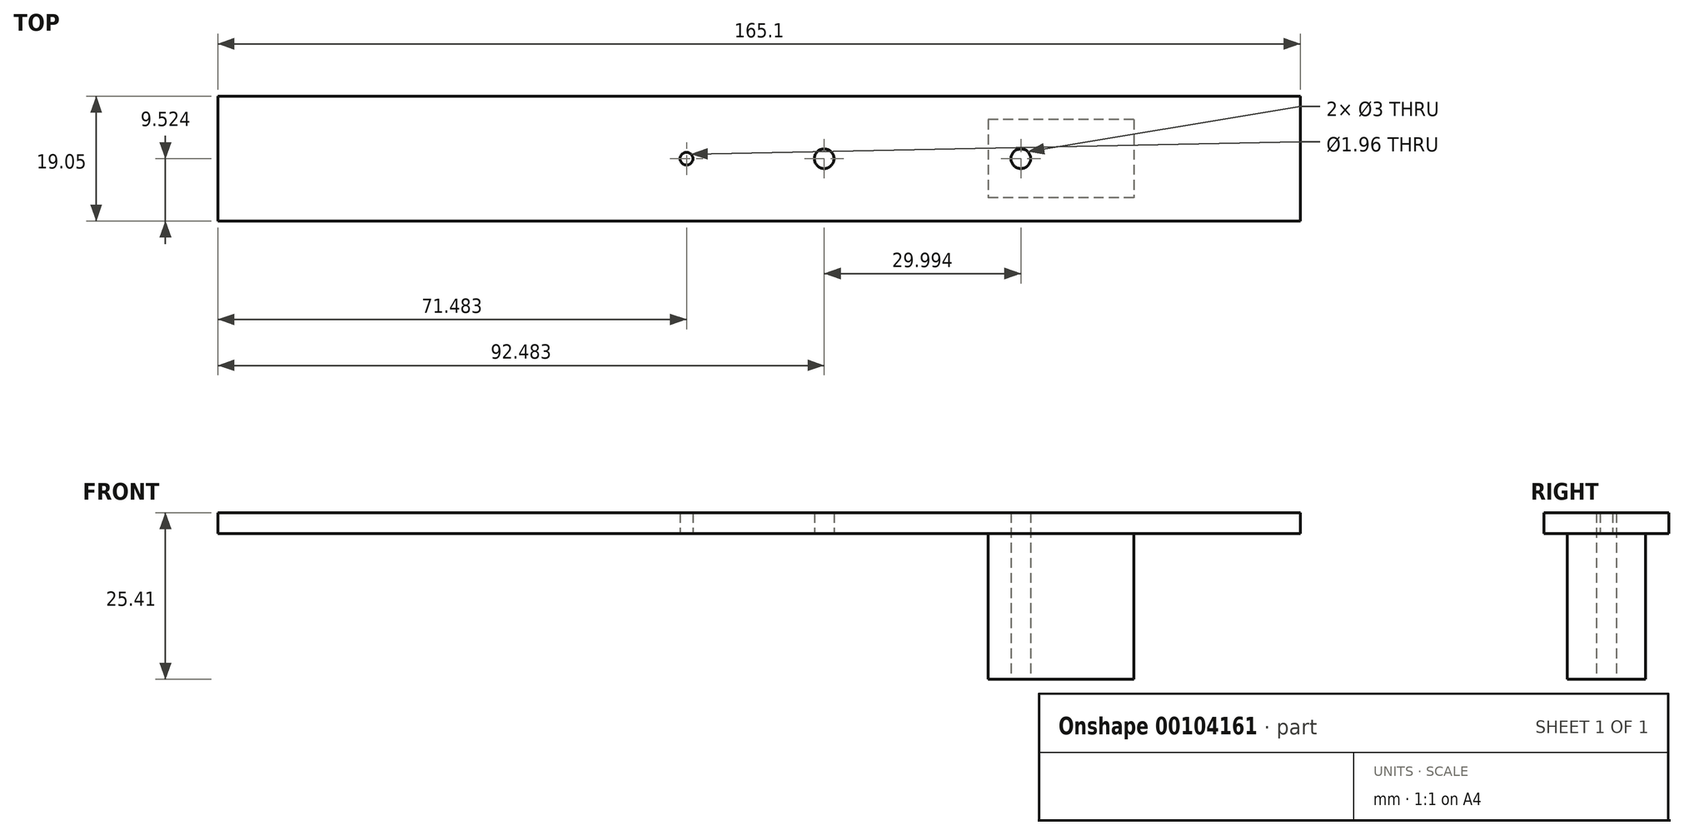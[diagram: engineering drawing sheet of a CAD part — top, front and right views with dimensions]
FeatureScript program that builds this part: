
annotation { "Feature Type Name" : "Feature", "Feature Type Description" : "" }
export const myFeature = defineFeature(function(context is Context, id is Id, definition is map)
    precondition{}
    {
        {
            var Q0;
            Q0=qCreatedBy(makeId("Top.planeOp"),FACE);
            var sketch = newSketch(context, id + "F0", { "sketchPlane" : qUnion([Q0])});
            skLineSegment(sketch, "E0.bottom", {"start": v(-131.62, -9.37) * mm, "end": v(33.48, -9.37) * mm});
            skLineSegment(sketch, "E0.top", {"start": v(-131.62, -28.42) * mm, "end": v(33.48, -28.42) * mm});
            skLineSegment(sketch, "E0.left", {"start": v(-131.62, -9.37) * mm, "end": v(-131.62, -28.42) * mm});
            skLineSegment(sketch, "E0.right", {"start": v(33.48, -9.37) * mm, "end": v(33.48, -28.42) * mm});
            skSolve(sketch);
        }
        {
            var Q0;
            Q0=makeQuery(id+"F0.imprint","IMPRINT",FACE,{"disambiguationData":[TD([[makeQuery(id+"F0.imprint","IMPRINT",EDGE,{"derivedFrom":sQuery(id+"F0.wireOp",EDGE,"E0.bottom")}),-1.0]])]});
            extrude(context, id + "F1", {"entities" : qUnion([Q0]), "depth" : 3.17 * mm});
        }
        {
            var Q0;
            Q0=makeQuery(id+"F1.opExtrude","CAP_FACE",FACE,{"disambiguationData":[OSD([sQuery(id+"F0.wireOp",EDGE,"E0.bottom"),sQuery(id+"F0.wireOp",EDGE,"E0.top"),sQuery(id+"F0.wireOp",EDGE,"E0.left"),sQuery(id+"F0.wireOp",EDGE,"E0.right")])],"isStart":true});
            var sketch = newSketch(context, id + "F2", { "sketchPlane" : qUnion([Q0])});
            skCircle(sketch, "E1", {"center": v(-39.14, 18.9) * mm, "radius": 1.5 * mm});
            skCircle(sketch, "E2", {"center": v(-60.14, 18.9) * mm, "radius": 0.98 * mm});
            skLineSegment(sketch, "E3.bottom", {"start": v(8.08, 12.93) * mm, "end": v(-14.14, 12.93) * mm});
            skLineSegment(sketch, "E3.top", {"start": v(8.08, 24.86) * mm, "end": v(-14.14, 24.86) * mm});
            skLineSegment(sketch, "E3.left", {"start": v(8.08, 12.93) * mm, "end": v(8.08, 24.86) * mm});
            skLineSegment(sketch, "E3.right", {"start": v(-14.14, 12.93) * mm, "end": v(-14.14, 24.86) * mm});
            skCircle(sketch, "E4", {"center": v(-9.14, 18.9) * mm, "radius": 1.5 * mm});
            skSolve(sketch);
        }
        {
            var Q0;
            Q0=makeQuery(id+"F2.imprint","IMPRINT",FACE,{"disambiguationData":[TD([[makeQuery(id+"F2.imprint","IMPRINT",EDGE,{"derivedFrom":sQuery(id+"F2.wireOp",EDGE,"E1")}),1.0]])]});
            extrude(context, id + "F3", {"entities" : qUnion([Q0]), "operationType" : NewBodyOperationType.REMOVE, "oppositeDirection" : true, "depth" : 25.4 * mm});
        }
        {
            var Q0;
            Q0=makeQuery(id+"F2.imprint","IMPRINT",FACE,{"disambiguationData":[TD([[makeQuery(id+"F2.imprint","IMPRINT",EDGE,{"derivedFrom":sQuery(id+"F2.wireOp",EDGE,"E2")}),1.0]])]});
            extrude(context, id + "F4", {"entities" : qUnion([Q0]), "operationType" : NewBodyOperationType.REMOVE, "oppositeDirection" : true, "depth" : 25.4 * mm});
        }
        {
            var Q0;
            Q0=makeQuery(id+"F2.imprint","IMPRINT",FACE,{"disambiguationData":[TD([[makeQuery(id+"F2.imprint","IMPRINT",EDGE,{"derivedFrom":sQuery(id+"F2.wireOp",EDGE,"E4")}),1.0]])]});
            extrude(context, id + "F5", {"entities" : qUnion([Q0]), "operationType" : NewBodyOperationType.REMOVE, "oppositeDirection" : true, "depth" : 25.4 * mm});
        }
        {
            var Q0;
            Q0=makeQuery(id+"F2.imprint","IMPRINT",FACE,{"disambiguationData":[TD([[makeQuery(id+"F2.imprint","IMPRINT",EDGE,{"derivedFrom":sQuery(id+"F2.wireOp",EDGE,"E3.bottom")}),-1.0]])]});
            extrude(context, id + "F6", {"entities" : qUnion([Q0]), "operationType" : NewBodyOperationType.ADD, "depth" : 22.22 * mm});
        }
    });
